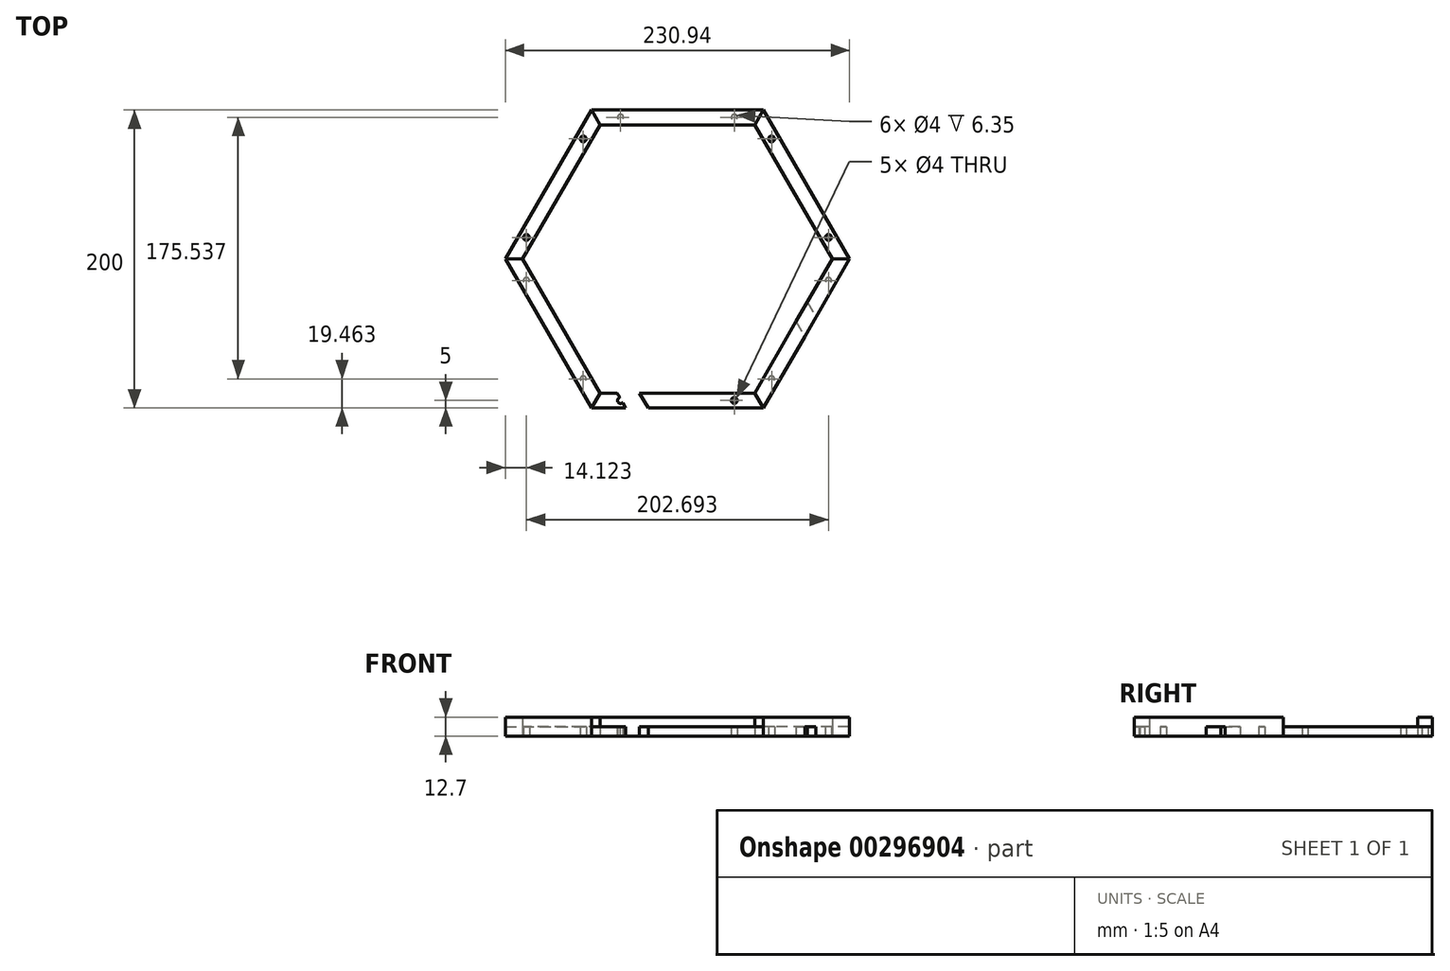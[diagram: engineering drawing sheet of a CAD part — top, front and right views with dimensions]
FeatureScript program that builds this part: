
annotation { "Feature Type Name" : "Feature", "Feature Type Description" : "" }
export const myFeature = defineFeature(function(context is Context, id is Id, definition is map)
    precondition{}
    {
        {
            var Q0;
            Q0=qCreatedBy(makeId("Top.planeOp"),FACE);
            var sketch = newSketch(context, id + "F0", { "sketchPlane" : qUnion([Q0])});
            skCircle(sketch, "E0", {"center": v(0, 0) * mm, "radius": 100 * mm});
            skCircle(sketch, "E1.cCircle", {"center": v(0, 0) * mm, "radius": 100 * mm, "construction": true});
            skLineSegment(sketch, "E1.0", {"start": v(-57.74, 100) * mm, "end": v(57.74, 100) * mm});
            skLineSegment(sketch, "E1.1", {"start": v(57.74, 100) * mm, "end": v(115.47, 0) * mm});
            skLineSegment(sketch, "E1.2", {"start": v(115.47, 0) * mm, "end": v(57.74, -100) * mm});
            skLineSegment(sketch, "E1.3", {"start": v(57.74, -100) * mm, "end": v(-57.74, -100) * mm});
            skLineSegment(sketch, "E1.4", {"start": v(-57.74, -100) * mm, "end": v(-115.47, 0) * mm});
            skLineSegment(sketch, "E1.5", {"start": v(-115.47, 0) * mm, "end": v(-57.74, 100) * mm});
            skPoint(sketch, "E1.0.midPoint", {"position": v(0, 100) * mm});
            skSolve(sketch);
        }
        {
            var Q0;
            Q0=qSketchRegion(id+"F0",true);
            extrude(context, id + "F1", {"entities" : qUnion([Q0]), "depth" : 6.35 * mm});
        }
        {
            var Q0;
            Q0=qCreatedBy(makeId("Top.planeOp"),FACE);
            var sketch = newSketch(context, id + "F2", { "sketchPlane" : qUnion([Q0])});
            skCircle(sketch, "E2.cCircle", {"center": v(0, 0) * mm, "radius": 95 * mm, "construction": true});
            skLineSegment(sketch, "E2.0", {"start": v(-54.85, 95) * mm, "end": v(54.85, 95) * mm, "construction": true});
            skLineSegment(sketch, "E2.1", {"start": v(54.85, 95) * mm, "end": v(109.7, 0) * mm, "construction": true});
            skLineSegment(sketch, "E2.2", {"start": v(109.7, 0) * mm, "end": v(54.85, -95) * mm, "construction": true});
            skLineSegment(sketch, "E2.3", {"start": v(54.85, -95) * mm, "end": v(-54.85, -95) * mm, "construction": true});
            skLineSegment(sketch, "E2.4", {"start": v(-54.85, -95) * mm, "end": v(-109.7, 0) * mm, "construction": true});
            skLineSegment(sketch, "E2.5", {"start": v(-109.7, 0) * mm, "end": v(-54.85, 95) * mm, "construction": true});
            skPoint(sketch, "E2.0.midPoint", {"position": v(0, 95) * mm});
            skPoint(sketch, "E3", {"position": v(38.15, 95) * mm});
            skPoint(sketch, "E4", {"position": v(-38.15, 95) * mm});
            skPoint(sketch, "E5", {"position": v(38.15, -95) * mm});
            skPoint(sketch, "E6", {"position": v(-38.15, -95) * mm});
            skPoint(sketch, "E7", {"position": v(-63.2, -80.54) * mm});
            skPoint(sketch, "E8", {"position": v(-101.35, -14.46) * mm});
            skPoint(sketch, "E9", {"position": v(-101.35, 14.46) * mm});
            skPoint(sketch, "E10", {"position": v(-63.2, 80.54) * mm});
            skPoint(sketch, "E11", {"position": v(63.2, 80.54) * mm});
            skPoint(sketch, "E12", {"position": v(101.35, 14.46) * mm});
            skPoint(sketch, "E13", {"position": v(101.35, -14.46) * mm});
            skPoint(sketch, "E14", {"position": v(63.2, -80.54) * mm});
            skCircle(sketch, "E15", {"center": v(38.15, 95) * mm, "radius": 2 * mm});
            skCircle(sketch, "E16", {"center": v(-38.15, 95) * mm, "radius": 2 * mm});
            skCircle(sketch, "E17", {"center": v(-63.2, 80.54) * mm, "radius": 2 * mm});
            skCircle(sketch, "E18", {"center": v(-101.35, 14.46) * mm, "radius": 2 * mm});
            skCircle(sketch, "E19", {"center": v(-101.35, -14.46) * mm, "radius": 2 * mm});
            skCircle(sketch, "E20", {"center": v(-63.2, -80.54) * mm, "radius": 2 * mm});
            skCircle(sketch, "E21", {"center": v(-38.15, -95) * mm, "radius": 2 * mm});
            skCircle(sketch, "E22", {"center": v(38.15, -95) * mm, "radius": 2 * mm});
            skCircle(sketch, "E23", {"center": v(63.2, -80.54) * mm, "radius": 2 * mm});
            skCircle(sketch, "E24", {"center": v(101.35, -14.46) * mm, "radius": 2 * mm});
            skCircle(sketch, "E25", {"center": v(101.35, 14.46) * mm, "radius": 2 * mm});
            skCircle(sketch, "E26", {"center": v(63.2, 80.54) * mm, "radius": 2 * mm});
            skCircle(sketch, "E27.cCircle", {"center": v(0, 0) * mm, "radius": 90 * mm, "construction": true});
            skLineSegment(sketch, "E27.0", {"start": v(-51.96, 90) * mm, "end": v(51.96, 90) * mm});
            skLineSegment(sketch, "E27.1", {"start": v(51.96, 90) * mm, "end": v(103.92, 0) * mm});
            skLineSegment(sketch, "E27.2", {"start": v(103.92, 0) * mm, "end": v(51.96, -90) * mm});
            skLineSegment(sketch, "E27.3", {"start": v(51.96, -90) * mm, "end": v(-51.96, -90) * mm});
            skLineSegment(sketch, "E27.4", {"start": v(-51.96, -90) * mm, "end": v(-103.92, 0) * mm});
            skLineSegment(sketch, "E27.5", {"start": v(-103.92, 0) * mm, "end": v(-51.96, 90) * mm});
            skPoint(sketch, "E27.0.midPoint", {"position": v(0, 90) * mm});
            skSolve(sketch);
        }
        {
            var Q0;
            Q0=qSketchRegion(id+"F2",true);
            extrude(context, id + "F3", {"entities" : qUnion([Q0]), "operationType" : NewBodyOperationType.REMOVE, "depth" : 20000 * mm});
        }
        {
            var Q0;
            Q0=makeQuery(id+"F1.opExtrude","CAP_FACE",FACE,{"disambiguationData":[OSD([sQuery(id+"F0.wireOp",EDGE,"E1.0"),sQuery(id+"F0.wireOp",EDGE,"E1.1"),sQuery(id+"F0.wireOp",EDGE,"E1.2"),sQuery(id+"F0.wireOp",EDGE,"E1.3"),sQuery(id+"F0.wireOp",EDGE,"E1.4"),sQuery(id+"F0.wireOp",EDGE,"E1.5")])],"isStart":false});
            var sketch = newSketch(context, id + "F4", { "sketchPlane" : qUnion([Q0])});
            skLineSegment(sketch, "E28", {"start": v(-51.96, -90) * mm, "end": v(-43.3, -85) * mm, "construction": true});
            skLineSegment(sketch, "E29", {"start": v(-43.3, -85) * mm, "end": v(-32.04, -78.5) * mm});
            skLineSegment(sketch, "E30", {"start": v(-32.04, -78.5) * mm, "end": v(-18.92, -101.22) * mm});
            skLineSegment(sketch, "E31", {"start": v(-43.3, -85) * mm, "end": v(-31.1, -106.13) * mm});
            skLineSegment(sketch, "E32", {"start": v(-31.1, -106.13) * mm, "end": v(-18.92, -101.22) * mm});
            skLineSegment(sketch, "E33", {"start": v(103.92, 0) * mm, "end": v(78.8, -14.5) * mm, "construction": true});
            skLineSegment(sketch, "E34", {"start": v(78.8, -14.5) * mm, "end": v(67.55, -21) * mm});
            skLineSegment(sketch, "E35", {"start": v(78.8, -14.5) * mm, "end": v(110.67, -69.68) * mm});
            skLineSegment(sketch, "E36", {"start": v(67.55, -21) * mm, "end": v(99.62, -76.55) * mm});
            skLineSegment(sketch, "E37", {"start": v(99.62, -76.55) * mm, "end": v(110.67, -69.68) * mm});
            skSolve(sketch);
        }
        {
            var Q0;
            Q0=qSketchRegion(id+"F4",true);
            extrude(context, id + "F5", {"entities" : qUnion([Q0]), "operationType" : NewBodyOperationType.REMOVE, "oppositeDirection" : true, "depth" : 25 * mm});
        }
        {
            var Q0;
            {var subQ0=sQuery(id+"F0.wireOp",EDGE,"E1.3");var subQ1=sQuery(id+"F0.wireOp",EDGE,"E1.2");var subQ3=makeQuery(id+"F1.opExtrude","CAP_EDGE",EDGE,{"disambiguationData":[OSD([subQ0])],"isStart":false});var subQ4=makeQuery(id+"F1.opExtrude","CAP_EDGE",EDGE,{"disambiguationData":[OSD([subQ1])],"isStart":false});var subQ5=makeQuery(id+"F4.imprint","INTERSECT",VERTEX,{"derivedFrom":[subQ4,subQ3]});Q0=makeQuery(id+"F4.imprint","IMPRINT",FACE,{"disambiguationData":[TD([[makeQuery(id+"F4.imprint","IMPRINT",EDGE,{"disambiguationData":[TD([[subQ5,1.0]])],"derivedFrom":subQ4}),-1.0]])]});}
            var sketch = newSketch(context, id + "F6", { "sketchPlane" : qUnion([Q0])});
            skLineSegment(sketch, "E38", {"start": v(-57.74, -100) * mm, "end": v(-51.96, -90) * mm});
            skLineSegment(sketch, "E39", {"start": v(115.47, 0) * mm, "end": v(103.92, 0) * mm});
            skLineSegment(sketch, "E40", {"start": v(51.96, 90) * mm, "end": v(57.74, 100) * mm});
            skLineSegment(sketch, "E41", {"start": v(-115.47, 0) * mm, "end": v(-103.92, 0) * mm});
            skLineSegment(sketch, "E42", {"start": v(-51.96, 90) * mm, "end": v(-57.74, 100) * mm});
            skLineSegment(sketch, "E43", {"start": v(57.74, -100) * mm, "end": v(51.96, -90) * mm});
            skLineSegment(sketch, "E44", {"start": v(-103.92, 0) * mm, "end": v(-51.96, -90) * mm});
            skLineSegment(sketch, "E45", {"start": v(-115.47, 0) * mm, "end": v(-57.74, -100) * mm});
            skLineSegment(sketch, "E46", {"start": v(51.96, -90) * mm, "end": v(103.92, 0) * mm});
            skLineSegment(sketch, "E47", {"start": v(115.47, 0) * mm, "end": v(57.74, -100) * mm});
            skLineSegment(sketch, "E48", {"start": v(-57.74, 100) * mm, "end": v(57.74, 100) * mm});
            skLineSegment(sketch, "E49", {"start": v(51.96, 90) * mm, "end": v(-51.96, 90) * mm});
            skSolve(sketch);
        }
        {
            var Q0;
            Q0=qSketchRegion(id+"F6",true);
            extrude(context, id + "F7", {"entities" : qUnion([Q0]), "operationType" : NewBodyOperationType.ADD, "depth" : 6.35 * mm});
        }
    });
